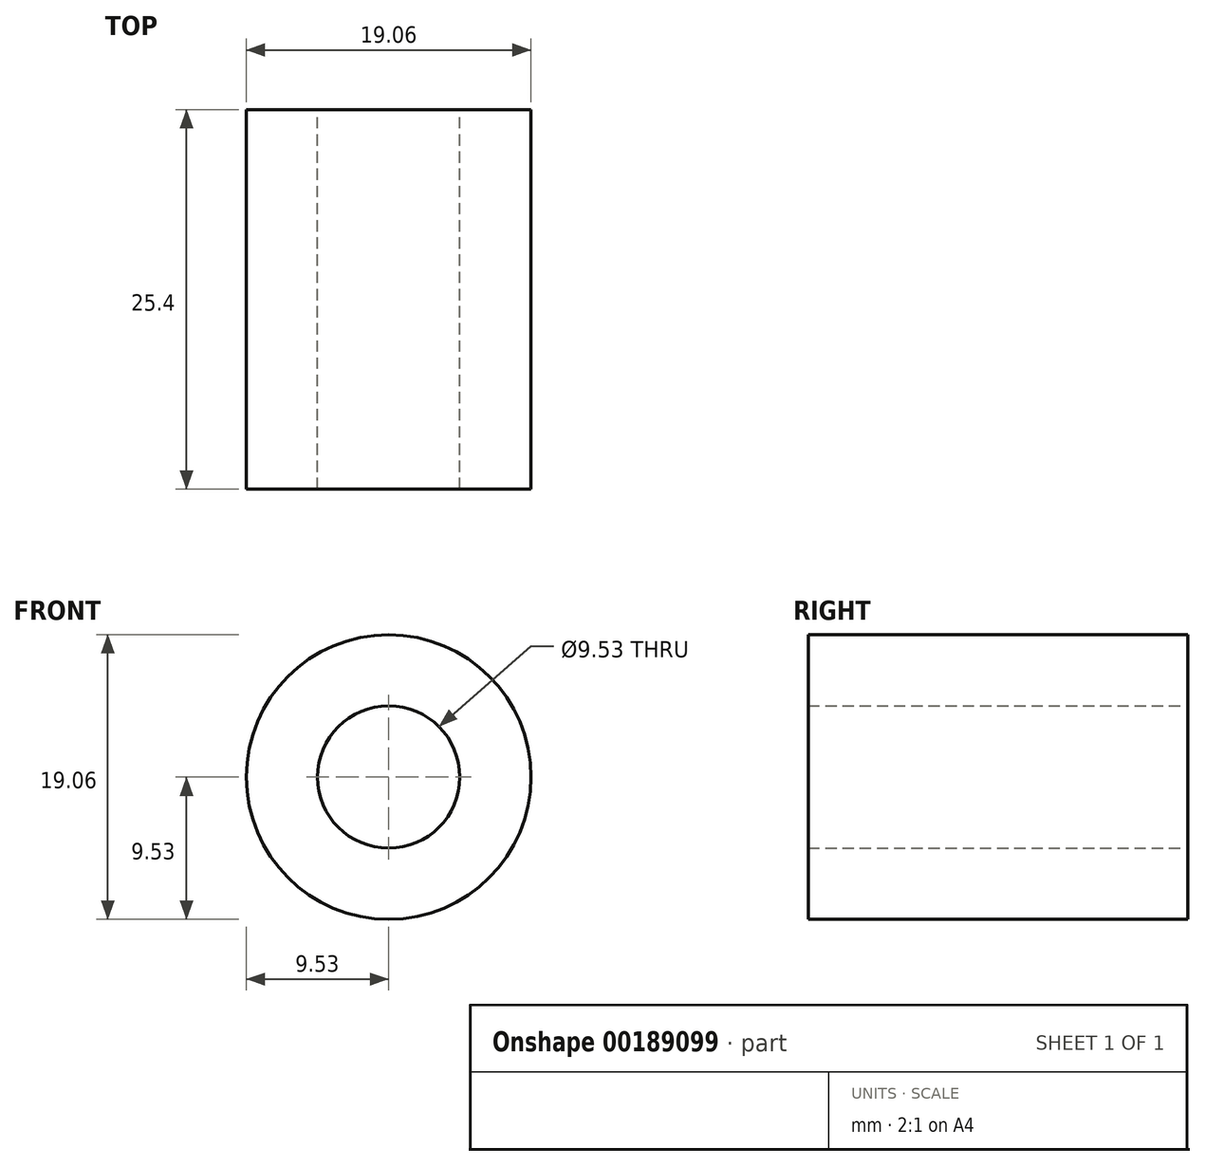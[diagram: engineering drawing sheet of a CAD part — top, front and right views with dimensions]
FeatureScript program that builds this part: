
annotation { "Feature Type Name" : "Feature", "Feature Type Description" : "" }
export const myFeature = defineFeature(function(context is Context, id is Id, definition is map)
    precondition{}
    {
        {
            var Q0;
            Q0=qCreatedBy(makeId("Front.planeOp"),FACE);
            var sketch = newSketch(context, id + "F0", { "sketchPlane" : qUnion([Q0])});
            skCircle(sketch, "E0", {"center": v(0, 0) * mm, "radius": 9.53 * mm});
            skSolve(sketch);
        }
        {
            var Q0;
            Q0 = qSketchRegion(id + "F0", true);
            extrude(context, id + "F1", {"entities" : qUnion([Q0]), "depth" : 25.4 * mm});
        }
        {
            var Q0;
            Q0=makeQuery(id+"F1.opExtrude","CAP_FACE",FACE,{"disambiguationData":[OSD([sQuery(id+"F0.wireOp",EDGE,"E0")])],"isStart":true});
            var sketch = newSketch(context, id + "F2", { "sketchPlane" : qUnion([Q0])});
            skLineSegment(sketch, "E1.bottom", {"start": v(4.76, 4.76) * mm, "end": v(-4.76, 4.76) * mm});
            skLineSegment(sketch, "E1.top", {"start": v(4.76, -4.76) * mm, "end": v(-4.76, -4.76) * mm});
            skLineSegment(sketch, "E1.left", {"start": v(4.76, 4.76) * mm, "end": v(4.76, -4.76) * mm});
            skLineSegment(sketch, "E1.right", {"start": v(-4.76, 4.76) * mm, "end": v(-4.76, -4.76) * mm});
            skPoint(sketch, "E1.middle", {"position": v(0, 0) * mm});
            skCircle(sketch, "E2", {"center": v(0, 0) * mm, "radius": 4.76 * mm});
            skSolve(sketch);
        }
        {
            var Q0;
            {var subQ0=sQuery(id+"F2.wireOp",EDGE,"E2");var subQ1=makeQuery(id+"F2.imprint","INTERSECT",VERTEX,{"derivedFrom":[sQuery(id+"F2.wireOp",EDGE,"E1.bottom"),subQ0]});Q0=makeQuery(id+"F2.imprint","IMPRINT",FACE,{"disambiguationData":[TD([[makeQuery(id+"F2.imprint","IMPRINT",EDGE,{"disambiguationData":[TD([[subQ1,1.0]])],"derivedFrom":subQ0}),1.0]])]});}
            extrude(context, id + "F3", {"entities" : qUnion([Q0]), "operationType" : NewBodyOperationType.REMOVE, "endBound" : BoundingType.THROUGH_ALL, "oppositeDirection" : true, "depth" : 25.4 * mm});
        }
    });
